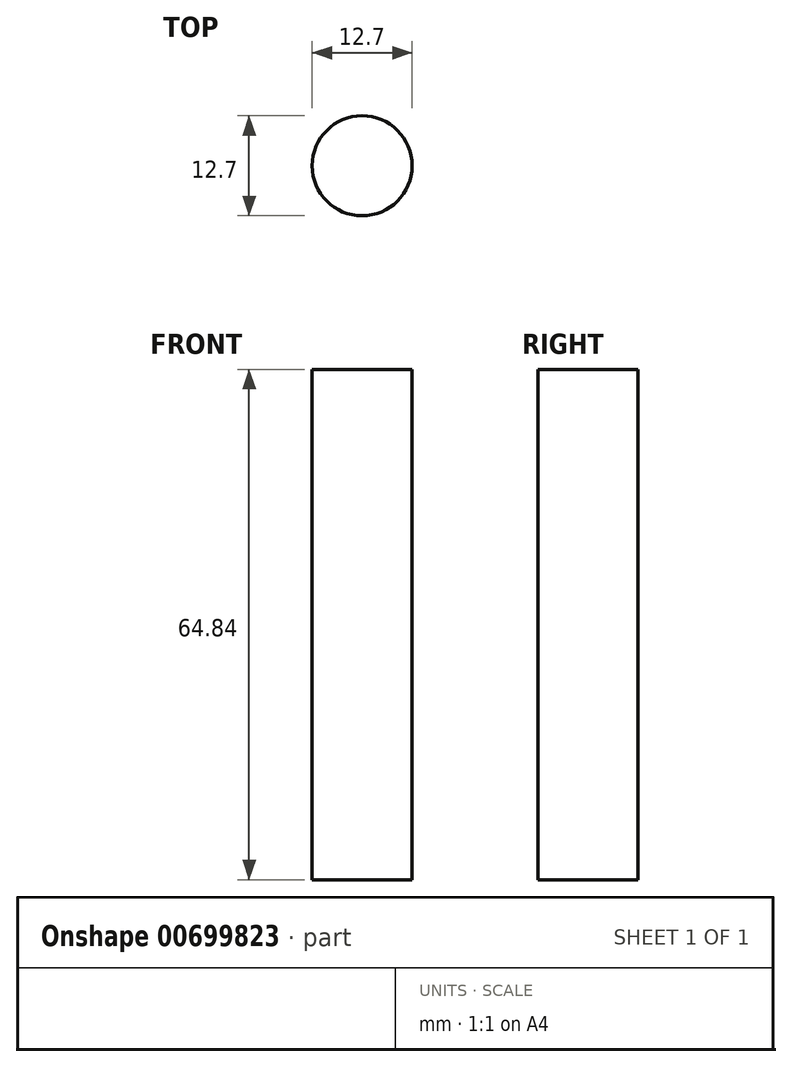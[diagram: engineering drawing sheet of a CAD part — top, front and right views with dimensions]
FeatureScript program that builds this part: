
annotation { "Feature Type Name" : "Feature", "Feature Type Description" : "" }
export const myFeature = defineFeature(function(context is Context, id is Id, definition is map)
    precondition{}
    {
        {
            var Q0;
            Q0=qCreatedBy(makeId("Top.planeOp"),FACE);
            var sketch = newSketch(context, id + "F0", { "sketchPlane" : qUnion([Q0])});
            skCircle(sketch, "E0", {"center": v(0, 0) * mm, "radius": 6.35 * mm});
            skSolve(sketch);
        }
        {
            var Q0;
            Q0=qSketchRegion(id+"F0",true);
            extrude(context, id + "F1", {"entities" : qUnion([Q0]), "depth" : 64.84 * mm});
        }
    });
